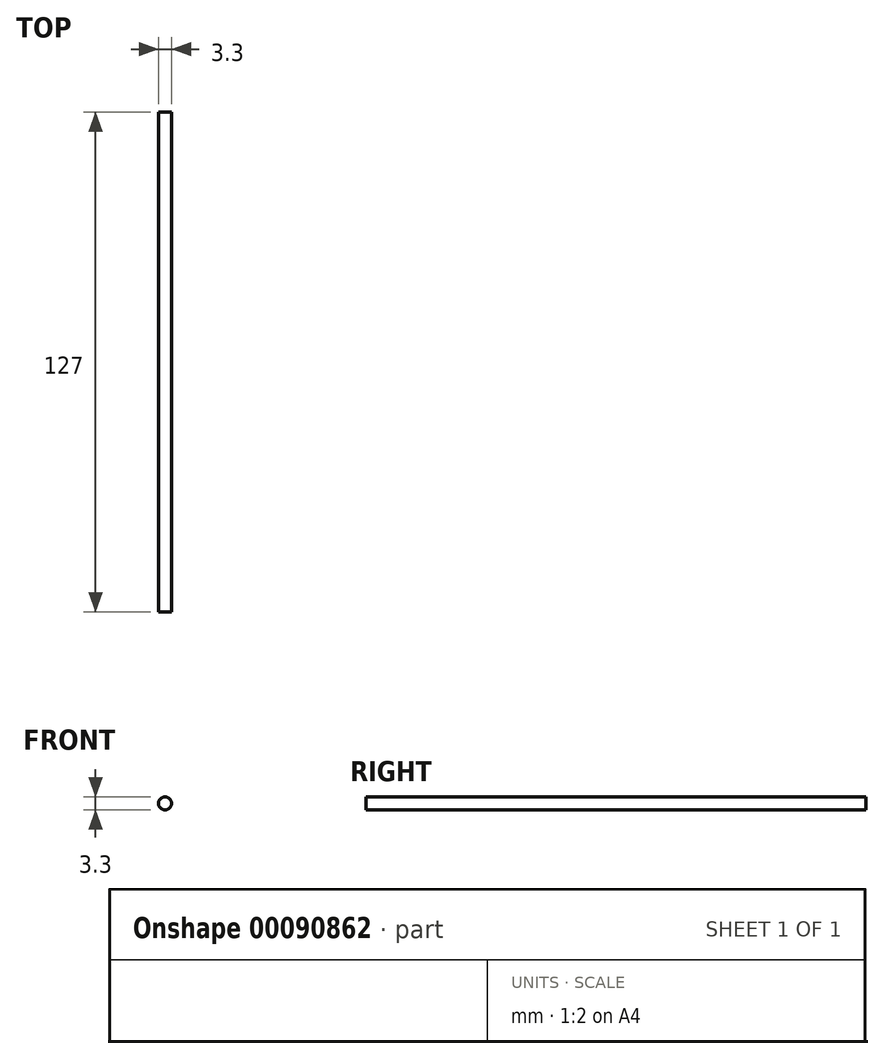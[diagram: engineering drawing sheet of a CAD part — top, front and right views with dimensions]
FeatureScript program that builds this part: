
annotation { "Feature Type Name" : "Feature", "Feature Type Description" : "" }
export const myFeature = defineFeature(function(context is Context, id is Id, definition is map)
    precondition{}
    {
        {
            var Q0;
            Q0=qCreatedBy(makeId("Front.planeOp"),FACE);
            var sketch = newSketch(context, id + "F0", { "sketchPlane" : qUnion([Q0])});
            skCircle(sketch, "E0", {"center": v(-17.5, 28.24) * mm, "radius": 1.65 * mm});
            skSolve(sketch);
        }
        {
            var Q0;
            Q0=makeQuery(id+"F0.imprint","IMPRINT",FACE,{"disambiguationData":[TD([[makeQuery(id+"F0.imprint","IMPRINT",EDGE,{"derivedFrom":sQuery(id+"F0.wireOp",EDGE,"E0")}),1.0]])]});
            extrude(context, id + "F1", {"entities" : qUnion([Q0]), "depth" : 127 * mm});
        }
    });
